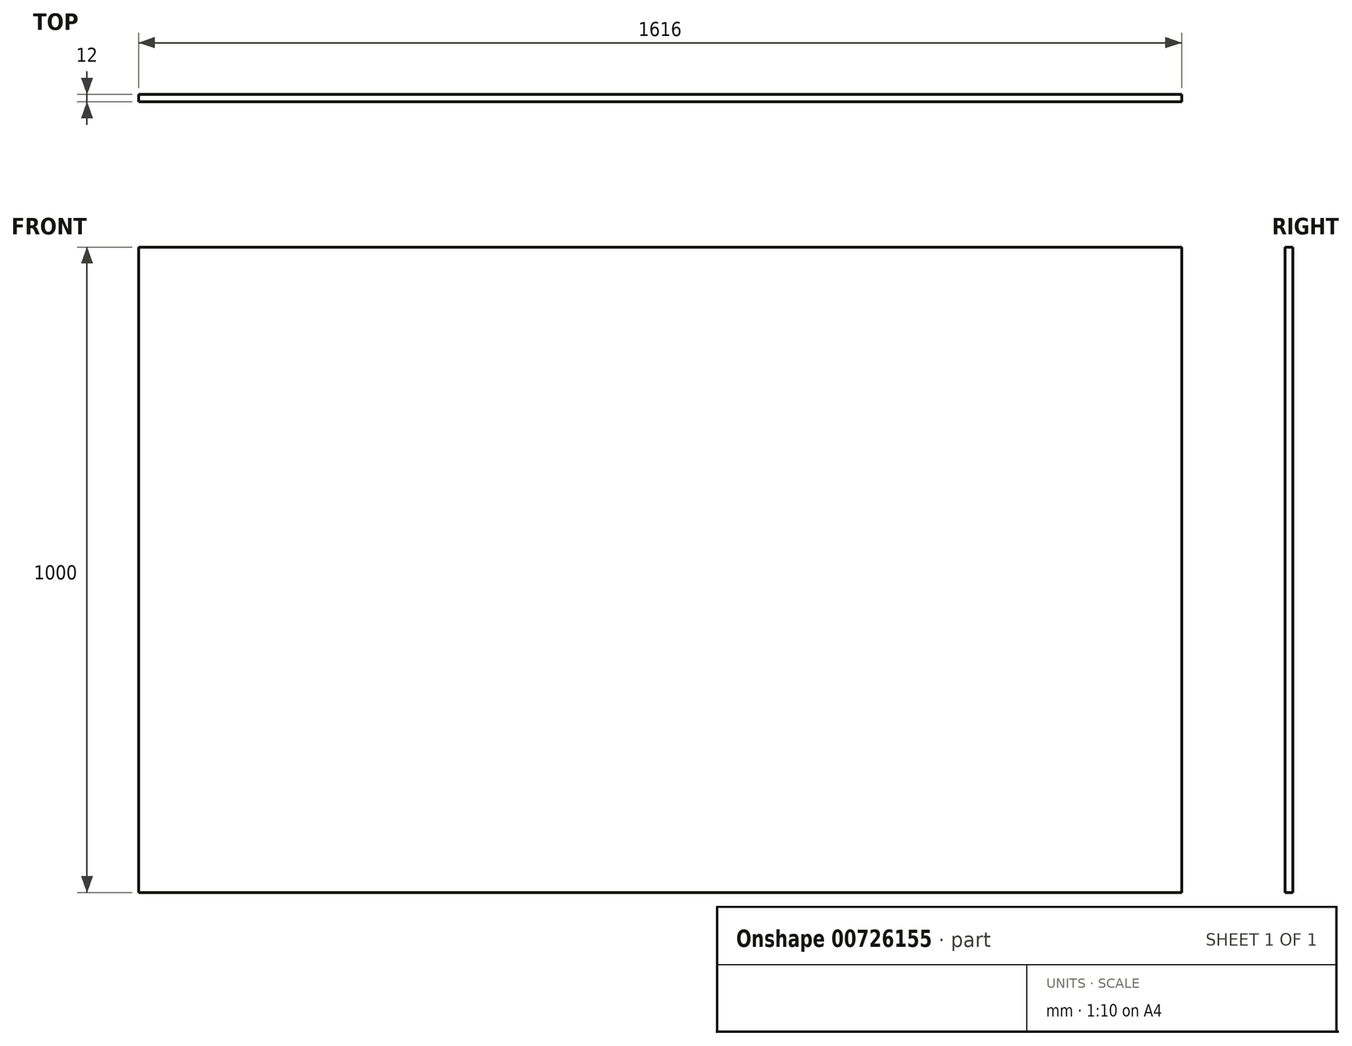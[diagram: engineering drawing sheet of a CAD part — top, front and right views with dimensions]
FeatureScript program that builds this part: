
annotation { "Feature Type Name" : "Feature", "Feature Type Description" : "" }
export const myFeature = defineFeature(function(context is Context, id is Id, definition is map)
    precondition{}
    {
        {
            var Q0;
            Q0=qCreatedBy(makeId("Front.planeOp"),FACE);
            var sketch = newSketch(context, id + "F0", { "sketchPlane" : qUnion([Q0])});
            skLineSegment(sketch, "E0.bottom", {"start": v(-808, 500) * mm, "end": v(808, 500) * mm});
            skLineSegment(sketch, "E0.top", {"start": v(-808, -500) * mm, "end": v(808, -500) * mm});
            skLineSegment(sketch, "E0.left", {"start": v(-808, 500) * mm, "end": v(-808, -500) * mm});
            skLineSegment(sketch, "E0.right", {"start": v(808, 500) * mm, "end": v(808, -500) * mm});
            skLineSegment(sketch, "E1", {"start": v(-808, 0) * mm, "end": v(808, 0) * mm, "construction": true});
            skSolve(sketch);
        }
        {
            var Q0;
            Q0 = qSketchRegion(id + "F0", true);
            extrude(context, id + "F1", {"entities" : qUnion([Q0]), "depth" : 12 * mm, "offsetDistance" : 25 * mm});
        }
    });
